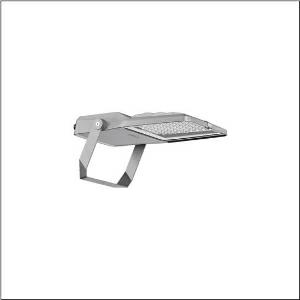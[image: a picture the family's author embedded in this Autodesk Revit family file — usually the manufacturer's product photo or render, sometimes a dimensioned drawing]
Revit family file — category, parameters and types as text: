
# Revit family: floodlight_fl_21_mini___pl43_5xa7776c2a1a_c133
name_source: partatom
category: Lighting Fixtures
units: mm (PartAtom-declared; Revit-internal decimal feet)

## family parameters
Cut with Voids When Loaded = No
Host = Face
Light Source = No
Part Type = Normal
Room Calculation Point = No
Round Connector Dimension = Use Diameter
Shared = No

## types (1)
- --- (1 x LED, 12500 lm, 89 W, 3000K)
    Apparent Load = 89 VA
    CIE Flux Codes = 27 78 99 100 100
    Color Rendering = 70
    Color Temperature = 3000K
    Default Elevation = 1800 mm
    Description = Floodlight FL 21 mini, floodlight, primary light control with lens, of PMMA, primary optical cover: protective disc, of toughened safety glass, transparent, light distribution: PL43, light emission: direct distribution, installation type: surface-mounted, LED, High Power LED, rated luminous flux: 12.500lm, luminous efficacy: 140lm/W, light colour: 730, colour temperature: 3000K, control gear: Smart Interface (Zhaga), control: flexible luminous flux parameterisation, time-dependent luminous flux control, constant luminous flux control, overheat protection, pre-setting: logarithmic dimming characteristic, with terminal, 6-pole, mains connection: 220..240V, AC, 50/60Hz, start of lifetime: 89W, end of service life: 94W, reduction: 43W, luminaire housing, of diecast aluminium, powder-coated, SITECO metallic grey (DB 702S), corrosivity category C5 mid according to DIN EN ISO 12944, suitable for swimming pools, chlorine-resistant, sealing non-destructively replaceable, mounting bracket, of steel, galvanised, powder-coated, SITECO metallic grey (DB 702S), Smart Interface below and above, protection rating (complete): IP66, insulation class (complete): insulation class II (safety insulation), certification: CE, ENEC, VDE, protection symbol: D, impact resistance: IK08, permissible operating ambient temperature: -40..+40°C, permissible operating ambient temperature for outdoor applications: -40..+50°C, standard: DIN EN 12944, LABS conformity tested according to VDMA 24364:2018-05, packaging unit: 1 piece

Light Distribution: PL43
    Height = 70 mm
    Lamp = 1 x LED
    Lamp Light Flux = 12500 lm
    Lamp Power = 89 W
    Lamp count = 1
    Length = 485 mm
    Luminous efficacy = 140 lm/W
    Manufacturer = Siteco
    ModVariant = No
    Model = 5XA7776C2A1A
    Number of Poles = 1
    OnlyDefault = Yes
    Power Factor = 1
    Product Name = Floodlight FL 21 mini | PL43
    Product group = floodlight | pylon annexe
    ProductGroupID = 6201
    Protection Class = Protection class II
    Protection Degree = IP 66
    RLX_Detail_Level = 1
    RLX_Emergency_Light_Flux = 0 lm
    RLX_Emergency_Type = 0
    RLX_Emergency_Type_DB = No
    RlxData = <blob elided: 95877 chars, md5=9e199662>
    Socket = socket
    Standby Power = 0 W
    System Light Flux = 12500 lm
    System Power = 89 W
    Type Comments = factory setting: luminous flux: 100 % | dim-lin: 254 | 456 mA
    Type Image = l_1006845.jpg
    URL = http://relux.com
    VarID = @adj_160617
    Voltage = 0 V
    Weight = 0.00 kg
    Width = 337 mm

## geometry (parser evidence)
native form markers: Blend x4, Sweep x13
no freeform markers — native parametric forms only
